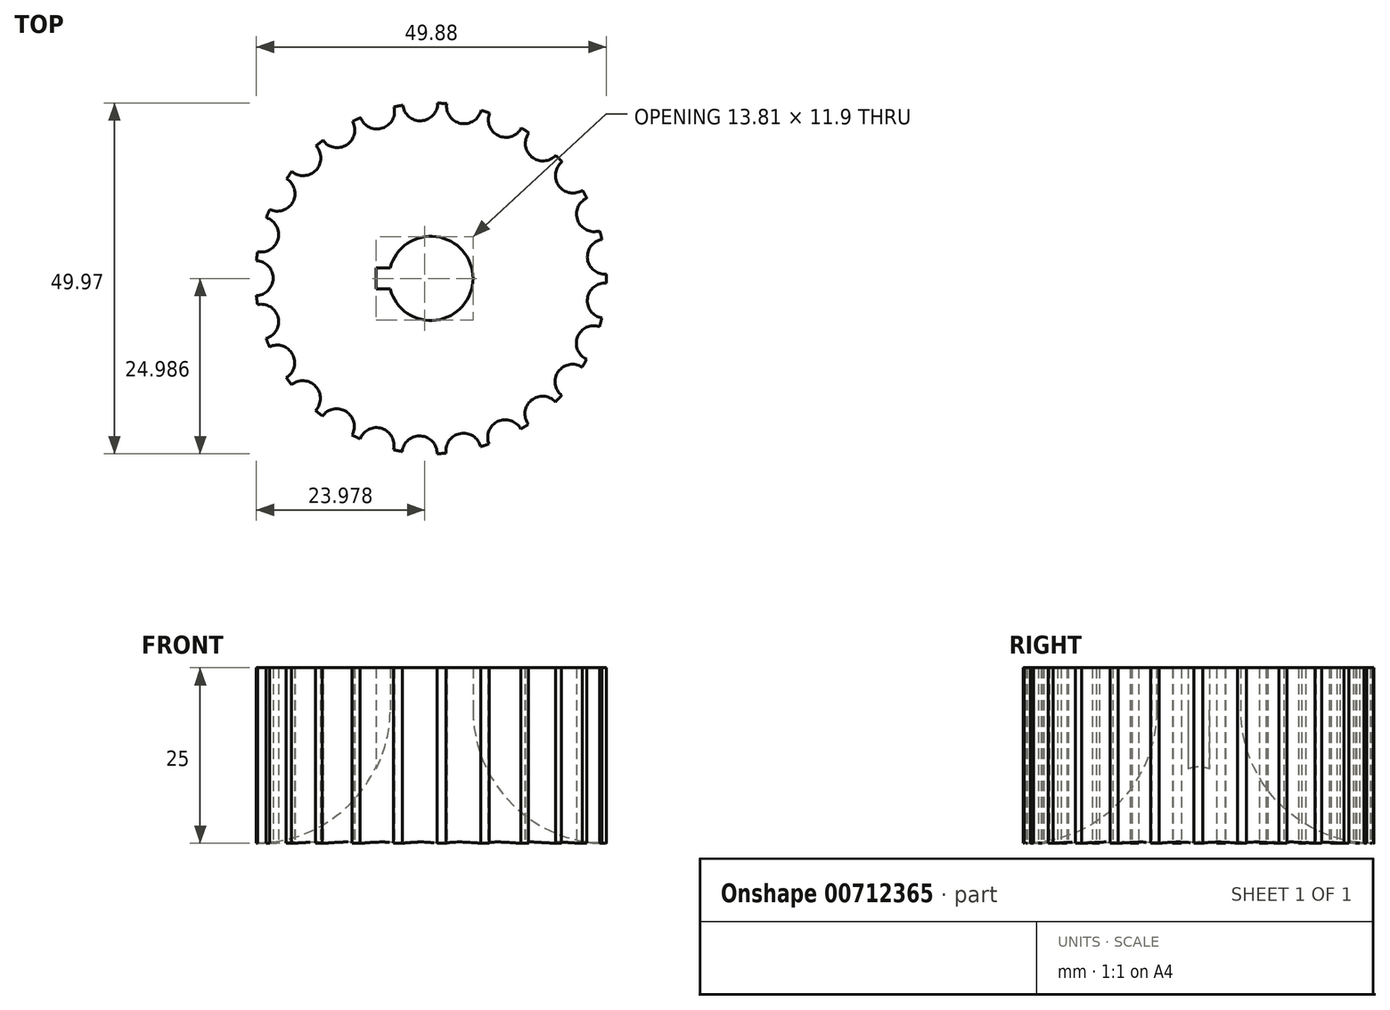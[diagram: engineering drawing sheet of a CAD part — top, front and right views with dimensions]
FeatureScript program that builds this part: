
annotation { "Feature Type Name" : "Feature", "Feature Type Description" : "" }
export const myFeature = defineFeature(function(context is Context, id is Id, definition is map)
    precondition{}
    {
        {
            var Q0;
            Q0=qCreatedBy(makeId("Top.planeOp"),FACE);
            var sketch = newSketch(context, id + "F0", { "sketchPlane" : qUnion([Q0])});
            skCircle(sketch, "E0", {"center": v(-13.12, -7.27) * mm, "radius": 25 * mm});
            skCircle(sketch, "E1", {"center": v(-14.64, 17.68) * mm, "radius": 2.5 * mm});
            skCircle(sketch, "E2.1.0", {"center": v(-20.8, 16.52) * mm, "radius": 2.5 * mm});
            skCircle(sketch, "E2.2.0", {"center": v(-26.48, 13.86) * mm, "radius": 2.5 * mm});
            skCircle(sketch, "E2.3.0", {"center": v(-31.31, 9.87) * mm, "radius": 2.5 * mm});
            skCircle(sketch, "E2.4.0", {"center": v(-35, 4.8) * mm, "radius": 2.5 * mm});
            skCircle(sketch, "E2.5.0", {"center": v(-37.32, -1.01) * mm, "radius": 2.5 * mm});
            skCircle(sketch, "E2.6.0", {"center": v(-38.12, -7.23) * mm, "radius": 2.5 * mm});
            skCircle(sketch, "E2.7.0", {"center": v(-37.34, -13.45) * mm, "radius": 2.5 * mm});
            skCircle(sketch, "E2.8.0", {"center": v(-35.05, -19.28) * mm, "radius": 2.5 * mm});
            skCircle(sketch, "E2.9.0", {"center": v(-31.37, -24.36) * mm, "radius": 2.5 * mm});
            skCircle(sketch, "E3.1.10.0", {"center": v(-26.55, -28.36) * mm, "radius": 2.5 * mm});
            skCircle(sketch, "E3.1.11.0", {"center": v(-20.88, -31.04) * mm, "radius": 2.5 * mm});
            skCircle(sketch, "E3.1.12.0", {"center": v(-14.73, -32.22) * mm, "radius": 2.5 * mm});
            skCircle(sketch, "E3.1.13.0", {"center": v(-8.48, -31.84) * mm, "radius": 2.5 * mm});
            skCircle(sketch, "E3.1.14.0", {"center": v(-2.51, -29.91) * mm, "radius": 2.5 * mm});
            skCircle(sketch, "E3.1.15.0", {"center": v(2.78, -26.56) * mm, "radius": 2.5 * mm});
            skCircle(sketch, "E3.1.16.0", {"center": v(7.08, -22) * mm, "radius": 2.5 * mm});
            skCircle(sketch, "E3.1.17.0", {"center": v(10.11, -16.52) * mm, "radius": 2.5 * mm});
            skCircle(sketch, "E3.1.18.0", {"center": v(11.68, -10.45) * mm, "radius": 2.5 * mm});
            skCircle(sketch, "E3.1.19.0", {"center": v(11.7, -4.18) * mm, "radius": 2.5 * mm});
            skCircle(sketch, "E4", {"center": v(-13.12, -7.27) * mm, "radius": 6 * mm});
            skLineSegment(sketch, "E5", {"start": v(-13.12, -7.27) * mm, "end": v(-19.12, -7.27) * mm});
            skLineSegment(sketch, "E6", {"start": v(-18.93, -5.77) * mm, "end": v(-18.93, -8.77) * mm});
            skLineSegment(sketch, "E7", {"start": v(-18.93, -5.77) * mm, "end": v(-20.93, -5.77) * mm});
            skLineSegment(sketch, "E8", {"start": v(-20.93, -5.77) * mm, "end": v(-20.93, -8.77) * mm});
            skLineSegment(sketch, "E9", {"start": v(-20.93, -8.77) * mm, "end": v(-18.93, -8.77) * mm});
            skCircle(sketch, "E10.1.20.0", {"center": v(10.14, 1.89) * mm, "radius": 2.5 * mm});
            skCircle(sketch, "E10.1.21.0", {"center": v(7.13, 7.39) * mm, "radius": 2.5 * mm});
            skCircle(sketch, "E10.1.22.0", {"center": v(2.85, 11.96) * mm, "radius": 2.5 * mm});
            skCircle(sketch, "E10.1.23.0", {"center": v(-2.43, 15.33) * mm, "radius": 2.5 * mm});
            skCircle(sketch, "E10.1.24.0", {"center": v(-8.4, 17.27) * mm, "radius": 2.5 * mm});
            skSolve(sketch);
        }
        {
            var Q0;
            {var subQ61=sQuery(id+"F0.wireOp",EDGE,"E7");Q0=makeQuery(id+"F0.imprint","IMPRINT",FACE,{"disambiguationData":[TD([[makeQuery(id+"F0.imprint","IMPRINT",EDGE,{"derivedFrom":subQ61}),-1.0]])]});}
            extrude(context, id + "F1", {"entities" : qUnion([Q0]), "depth" : 25 * mm, "offsetDistance" : 25 * mm});
        }
        {
            var Q0;
            Q0=makeQuery(id+"F1.opExtrude","CAP_EDGE",EDGE,{"disambiguationData":[OSD([sQuery(id+"F0.wireOp",EDGE,"E4")])],"isStart":true});
            fillet(context, id + "F2", {"entities" : qUnion([Q0]), "radius" : 19 * mm, "tangentPropagation" : true, "allowEdgeOverflow" : false});
        }
    });
